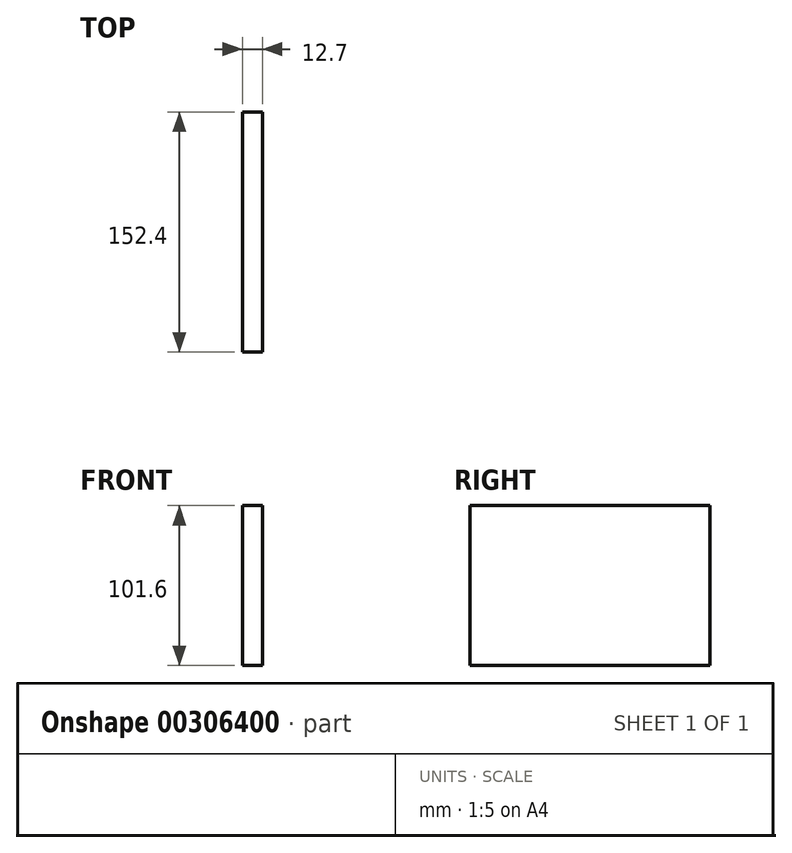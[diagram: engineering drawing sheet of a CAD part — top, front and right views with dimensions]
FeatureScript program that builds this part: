
annotation { "Feature Type Name" : "Feature", "Feature Type Description" : "" }
export const myFeature = defineFeature(function(context is Context, id is Id, definition is map)
    precondition{}
    {
        {
            var Q0;
            Q0=qCreatedBy(makeId("Right.planeOp"),FACE);
            var sketch = newSketch(context, id + "F0", { "sketchPlane" : qUnion([Q0])});
            skLineSegment(sketch, "E0.bottom", {"start": v(-76.2, -50.8) * mm, "end": v(76.2, -50.8) * mm});
            skLineSegment(sketch, "E0.top", {"start": v(-76.2, 50.8) * mm, "end": v(76.2, 50.8) * mm});
            skLineSegment(sketch, "E0.left", {"start": v(-76.2, -50.8) * mm, "end": v(-76.2, 50.8) * mm});
            skLineSegment(sketch, "E0.right", {"start": v(76.2, -50.8) * mm, "end": v(76.2, 50.8) * mm});
            skPoint(sketch, "E0.middle", {"position": v(0, 0) * mm});
            skSolve(sketch);
        }
        {
            var Q0;
            Q0 = qSketchRegion(id + "F0", true);
            extrude(context, id + "F1", {"entities" : qUnion([Q0]), "depth" : 12.7 * mm});
        }
    });
